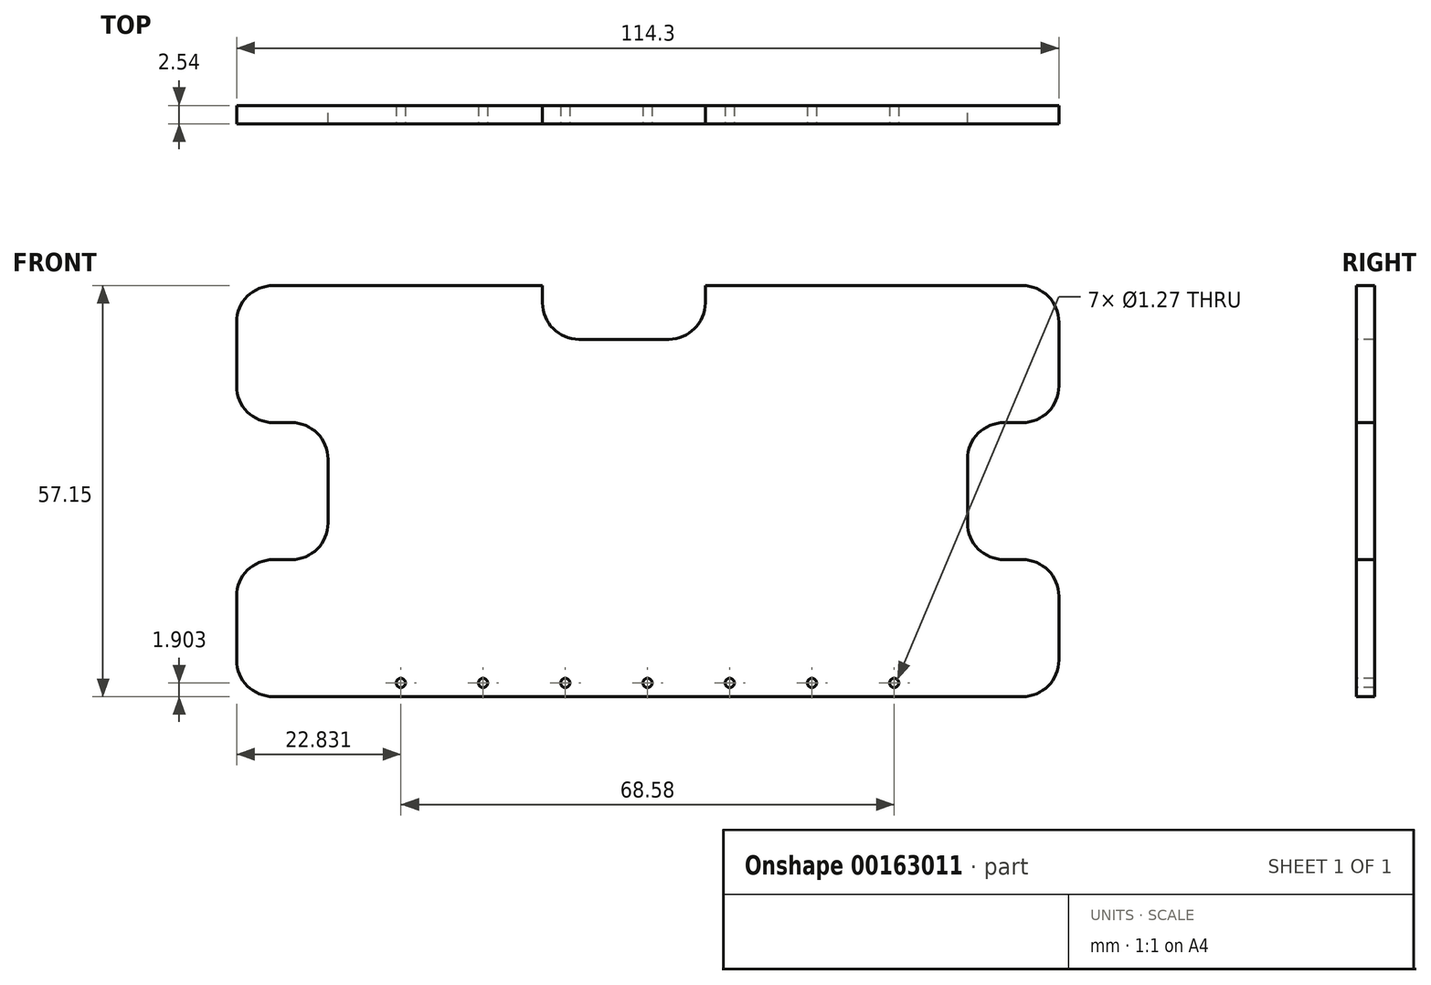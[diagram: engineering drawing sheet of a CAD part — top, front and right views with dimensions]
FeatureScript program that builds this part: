
annotation { "Feature Type Name" : "Feature", "Feature Type Description" : "" }
export const myFeature = defineFeature(function(context is Context, id is Id, definition is map)
    precondition{}
    {
        {
            var Q0;
            Q0=qCreatedBy(makeId("Front.planeOp"),FACE);
            var sketch = newSketch(context, id + "F0", { "sketchPlane" : qUnion([Q0])});
            skLineSegment(sketch, "E0", {"start": v(-65.75, 56.6) * mm, "end": v(48.55, 56.6) * mm});
            skLineSegment(sketch, "E1", {"start": v(-65.75, 56.6) * mm, "end": v(-65.75, 37.56) * mm});
            skLineSegment(sketch, "E2", {"start": v(48.55, 56.6) * mm, "end": v(48.55, 37.56) * mm});
            skLineSegment(sketch, "E3", {"start": v(-65.75, 37.56) * mm, "end": v(-53.05, 37.56) * mm});
            skLineSegment(sketch, "E4", {"start": v(48.55, 37.56) * mm, "end": v(35.85, 37.56) * mm});
            skLineSegment(sketch, "E5", {"start": v(-53.05, 37.56) * mm, "end": v(-53.05, 18.5) * mm});
            skLineSegment(sketch, "E6", {"start": v(35.85, 37.56) * mm, "end": v(35.85, 18.5) * mm});
            skLineSegment(sketch, "E7", {"start": v(-53.05, 18.5) * mm, "end": v(-65.75, 18.5) * mm});
            skLineSegment(sketch, "E8", {"start": v(35.85, 18.5) * mm, "end": v(48.55, 18.5) * mm});
            skLineSegment(sketch, "E9", {"start": v(-65.75, 18.5) * mm, "end": v(-65.75, -0.54) * mm});
            skLineSegment(sketch, "E10", {"start": v(48.55, 18.5) * mm, "end": v(48.55, -0.54) * mm});
            skLineSegment(sketch, "E11", {"start": v(-65.75, -0.54) * mm, "end": v(48.55, -0.54) * mm});
            skSolve(sketch);
        }
        {
            var Q0;
            Q0 = qSketchRegion(id + "F0", true);
            extrude(context, id + "F1", {"entities" : qUnion([Q0]), "depth" : 2.54 * mm});
        }
        {
            var Q0;
            Q0=makeQuery(id+"F1.opExtrude","SWEPT_EDGE",EDGE,{"disambiguationData":[OSD([sQuery(id+"F0.wireOp",EDGE,"E0"),sQuery(id+"F0.wireOp",EDGE,"E1")])]});
            var Q1;
            Q1=makeQuery(id+"F1.opExtrude","SWEPT_EDGE",EDGE,{"disambiguationData":[OSD([sQuery(id+"F0.wireOp",EDGE,"E1"),sQuery(id+"F0.wireOp",EDGE,"E3")])]});
            var Q2;
            Q2=makeQuery(id+"F1.opExtrude","SWEPT_EDGE",EDGE,{"disambiguationData":[OSD([sQuery(id+"F0.wireOp",EDGE,"E3"),sQuery(id+"F0.wireOp",EDGE,"E5")])]});
            var Q3;
            Q3=makeQuery(id+"F1.opExtrude","SWEPT_EDGE",EDGE,{"disambiguationData":[OSD([sQuery(id+"F0.wireOp",EDGE,"E5"),sQuery(id+"F0.wireOp",EDGE,"E7")])]});
            var Q4;
            Q4=makeQuery(id+"F1.opExtrude","SWEPT_EDGE",EDGE,{"disambiguationData":[OSD([sQuery(id+"F0.wireOp",EDGE,"E7"),sQuery(id+"F0.wireOp",EDGE,"E9")])]});
            var Q5;
            Q5=makeQuery(id+"F1.opExtrude","SWEPT_EDGE",EDGE,{"disambiguationData":[OSD([sQuery(id+"F0.wireOp",EDGE,"E9"),sQuery(id+"F0.wireOp",EDGE,"E11")])]});
            var Q6;
            Q6=makeQuery(id+"F1.opExtrude","SWEPT_EDGE",EDGE,{"disambiguationData":[OSD([sQuery(id+"F0.wireOp",EDGE,"E10"),sQuery(id+"F0.wireOp",EDGE,"E11")])]});
            var Q7;
            Q7=makeQuery(id+"F1.opExtrude","SWEPT_EDGE",EDGE,{"disambiguationData":[OSD([sQuery(id+"F0.wireOp",EDGE,"E6"),sQuery(id+"F0.wireOp",EDGE,"E8")])]});
            var Q8;
            Q8=makeQuery(id+"F1.opExtrude","SWEPT_EDGE",EDGE,{"disambiguationData":[OSD([sQuery(id+"F0.wireOp",EDGE,"E8"),sQuery(id+"F0.wireOp",EDGE,"E10")])]});
            var Q9;
            Q9=makeQuery(id+"F1.opExtrude","SWEPT_EDGE",EDGE,{"disambiguationData":[OSD([sQuery(id+"F0.wireOp",EDGE,"E4"),sQuery(id+"F0.wireOp",EDGE,"E6")])]});
            var Q10;
            Q10=makeQuery(id+"F1.opExtrude","SWEPT_EDGE",EDGE,{"disambiguationData":[OSD([sQuery(id+"F0.wireOp",EDGE,"E2"),sQuery(id+"F0.wireOp",EDGE,"E4")])]});
            var Q11;
            Q11=makeQuery(id+"F1.opExtrude","SWEPT_EDGE",EDGE,{"disambiguationData":[OSD([sQuery(id+"F0.wireOp",EDGE,"E0"),sQuery(id+"F0.wireOp",EDGE,"E2")])]});
            fillet(context, id + "F2", {"entities" : qUnion([Q0, Q1, Q2, Q3, Q4, Q5, Q6, Q7, Q8, Q9, Q10, Q11]), "radius" : 5.08 * mm, "tangentPropagation" : true, "allowEdgeOverflow" : false});
        }
        {
            var Q0;
            Q0=makeQuery(id+"F1.opExtrude","CAP_FACE",FACE,{"disambiguationData":[OSD([sQuery(id+"F0.wireOp",EDGE,"E0"),sQuery(id+"F0.wireOp",EDGE,"E1"),sQuery(id+"F0.wireOp",EDGE,"E2"),sQuery(id+"F0.wireOp",EDGE,"E3"),sQuery(id+"F0.wireOp",EDGE,"E4"),sQuery(id+"F0.wireOp",EDGE,"E5"),sQuery(id+"F0.wireOp",EDGE,"E6"),sQuery(id+"F0.wireOp",EDGE,"E7"),sQuery(id+"F0.wireOp",EDGE,"E8"),sQuery(id+"F0.wireOp",EDGE,"E9"),sQuery(id+"F0.wireOp",EDGE,"E10"),sQuery(id+"F0.wireOp",EDGE,"E11")])],"isStart":false});
            var sketch = newSketch(context, id + "F3", { "sketchPlane" : qUnion([Q0])});
            skCircle(sketch, "E12", {"center": v(-42.92, 1.36) * mm, "radius": 0.64 * mm});
            skCircle(sketch, "E13.1.0.0", {"center": v(-31.49, 1.36) * mm, "radius": 0.64 * mm});
            skCircle(sketch, "E13.2.0.0", {"center": v(-20.06, 1.36) * mm, "radius": 0.64 * mm});
            skCircle(sketch, "E14.1.0.0", {"center": v(-8.63, 1.36) * mm, "radius": 0.64 * mm});
            skCircle(sketch, "E14.2.0.0", {"center": v(2.8, 1.36) * mm, "radius": 0.64 * mm});
            skCircle(sketch, "E15.1.0.0", {"center": v(14.23, 1.36) * mm, "radius": 0.64 * mm});
            skCircle(sketch, "E15.2.0.0", {"center": v(25.66, 1.36) * mm, "radius": 0.64 * mm});
            skSolve(sketch);
        }
        {
            var Q0;
            Q0 = qSketchRegion(id + "F3", true);
            extrude(context, id + "F4", {"entities" : qUnion([Q0]), "operationType" : NewBodyOperationType.REMOVE, "oppositeDirection" : true, "depth" : 25.4 * mm});
        }
        {
            var Q0;
            Q0=makeQuery(id+"F1.opExtrude","CAP_FACE",FACE,{"disambiguationData":[OSD([sQuery(id+"F0.wireOp",EDGE,"E0"),sQuery(id+"F0.wireOp",EDGE,"E1"),sQuery(id+"F0.wireOp",EDGE,"E2"),sQuery(id+"F0.wireOp",EDGE,"E3"),sQuery(id+"F0.wireOp",EDGE,"E4"),sQuery(id+"F0.wireOp",EDGE,"E5"),sQuery(id+"F0.wireOp",EDGE,"E6"),sQuery(id+"F0.wireOp",EDGE,"E7"),sQuery(id+"F0.wireOp",EDGE,"E8"),sQuery(id+"F0.wireOp",EDGE,"E9"),sQuery(id+"F0.wireOp",EDGE,"E10"),sQuery(id+"F0.wireOp",EDGE,"E11")])],"isStart":false});
            var sketch = newSketch(context, id + "F5", { "sketchPlane" : qUnion([Q0])});
            skLineSegment(sketch, "E16", {"start": v(-23.23, 56.6) * mm, "end": v(-23.23, 49.13) * mm});
            skLineSegment(sketch, "E17", {"start": v(-23.23, 49.13) * mm, "end": v(-0.61, 49.13) * mm});
            skLineSegment(sketch, "E18", {"start": v(-0.61, 49.13) * mm, "end": v(-0.61, 56.6) * mm});
            skSolve(sketch);
        }
        {
            var Q0;
            Q0 = qSketchRegion(id + "F5", true);
            var Q1;
            {var subQ0=sQuery(id+"F5.wireOp",EDGE,"E16");Q1=makeQuery(id+"F5.imprint","IMPRINT",FACE,{"disambiguationData":[TD([[makeQuery(id+"F5.imprint","IMPRINT",EDGE,{"derivedFrom":subQ0}),1.0]])]});}
            extrude(context, id + "F6", {"entities" : qUnion([Q0, Q1]), "operationType" : NewBodyOperationType.REMOVE, "oppositeDirection" : true, "depth" : 25.4 * mm});
        }
        {
            var Q0;
            Q0=makeQuery(id+"F6.boolean.opBoolean","COPY",EDGE,{"derivedFrom":makeQuery(id+"F6.opExtrude","SWEPT_EDGE",EDGE,{"disambiguationData":[OSD([sQuery(id+"F5.wireOp",EDGE,"E16"),sQuery(id+"F5.wireOp",EDGE,"E17")])]})});
            var Q1;
            Q1=makeQuery(id+"F6.boolean.opBoolean","COPY",EDGE,{"derivedFrom":makeQuery(id+"F6.opExtrude","SWEPT_EDGE",EDGE,{"disambiguationData":[OSD([sQuery(id+"F5.wireOp",EDGE,"E17"),sQuery(id+"F5.wireOp",EDGE,"E18")])]})});
            fillet(context, id + "F7", {"entities" : qUnion([Q0, Q1]), "radius" : 5.08 * mm, "tangentPropagation" : true, "allowEdgeOverflow" : false});
        }
    });
